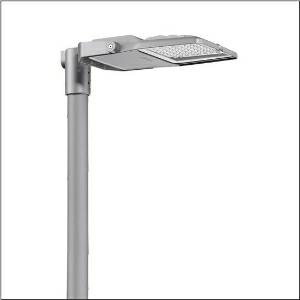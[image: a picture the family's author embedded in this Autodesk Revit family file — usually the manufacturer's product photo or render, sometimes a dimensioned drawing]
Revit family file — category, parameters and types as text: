
# Revit family: floodlight_fl_21_mini___pl33t_5xa7771b4f3a_f122
name_source: partatom
category: Lighting Fixtures
units: mm (PartAtom-declared; Revit-internal decimal feet)

## family parameters
Cut with Voids When Loaded = No
Host = Face
Light Source = No
Part Type = Normal
Room Calculation Point = No
Round Connector Dimension = Use Diameter
Shared = No

## types (1)
- --- (1 x LED, 6420 lm, 45.5 W, 4000K)
    Apparent Load = 46 VA
    CIE Flux Codes = 26 75 99 100 100
    Color Rendering = 70
    Color Temperature = 4000K
    Default Elevation = 1800 mm
    Description = Floodlight FL 21 mini, floodlight, primary light control with lens, of PMMA, primary optical cover: protective disc, of toughened safety glass, transparent, light distribution: PL33T, light emission: direct distribution, installation type: surface-mounted, LED, High Power LED, rated luminous flux: 6.420lm, luminous efficacy: 141lm/W, light colour: 740, colour temperature: 4000K, control gear: ECG iQ, control: Auto-Match, Temp-Guard, Lumen-Switch, Night-Set, Smart-Wire, Light-Fading, Desk-Remote (wireless, voltage-free reading and setting of iQ features in the workshop via application-optimized NFC function/RFID function), optimised constant luminous flux control (CLO 2.0), with terminal, 6-pole, mains connection: 220..240V, AC, 50/60Hz, start of lifetime: 46W, end of lifetime: 48W, reduction: 22W, luminaire housing, of diecast aluminium, powder-coated, Siteco® metallic grey (DB 702S), corrosivity category C5 according to DIN EN ISO 12944, mast bracket, of steel, galvanised, powder-coated, Siteco® metallic grey (DB 702S), protection rating (complete): IP66, insulation class (complete): insulation class II (safety insulation), certification: CE, ENEC, VDE, protection symbol: D, impact resistance: IK08, permissible operating ambient temperature: -40..+40°C, permissible operating ambient temperature for outdoor applications: -40..+50°C, standard: DIN EN 12944, packaging unit: 1 piece

Light Distribution: PL33T
    Height = 70 mm
    Lamp = 1 x LED
    Lamp Light Flux = 6420 lm
    Lamp Power = 45.5 W
    Lamp count = 1
    Length = 485 mm
    Luminous efficacy = 141 lm/W
    Manufacturer = Siteco
    ModVariant = No
    Model = 5XA7771B4F3A
    Number of Poles = 1
    OnlyDefault = Yes
    Power Factor = 1
    Product Name = Floodlight FL 21 mini | PL33T
    Product group = floodlight | pylon top
    ProductGroupID = 6101
    Protection Class = Protection class II
    Protection Degree = IP 66
    RLX_Detail_Level = 1
    RlxData = <blob elided: 100853 chars, md5=a898e0f9>
    Socket = socket
    Standby Power = 0 W
    System Light Flux = 6420 lm
    System Power = 46 W
    Type Comments = factory setting: luminous flux: 100 % | dim-lin: 254 | 463 mA
    Type Image = l_1007125.jpg
    URL = http://relux.com
    VarID = @adj_060197
    Voltage = 0 V
    Weight = 0.00 kg
    Width = 337 mm

## geometry (parser evidence)
native form markers: Blend x4, Sweep x14
no freeform markers — native parametric forms only
